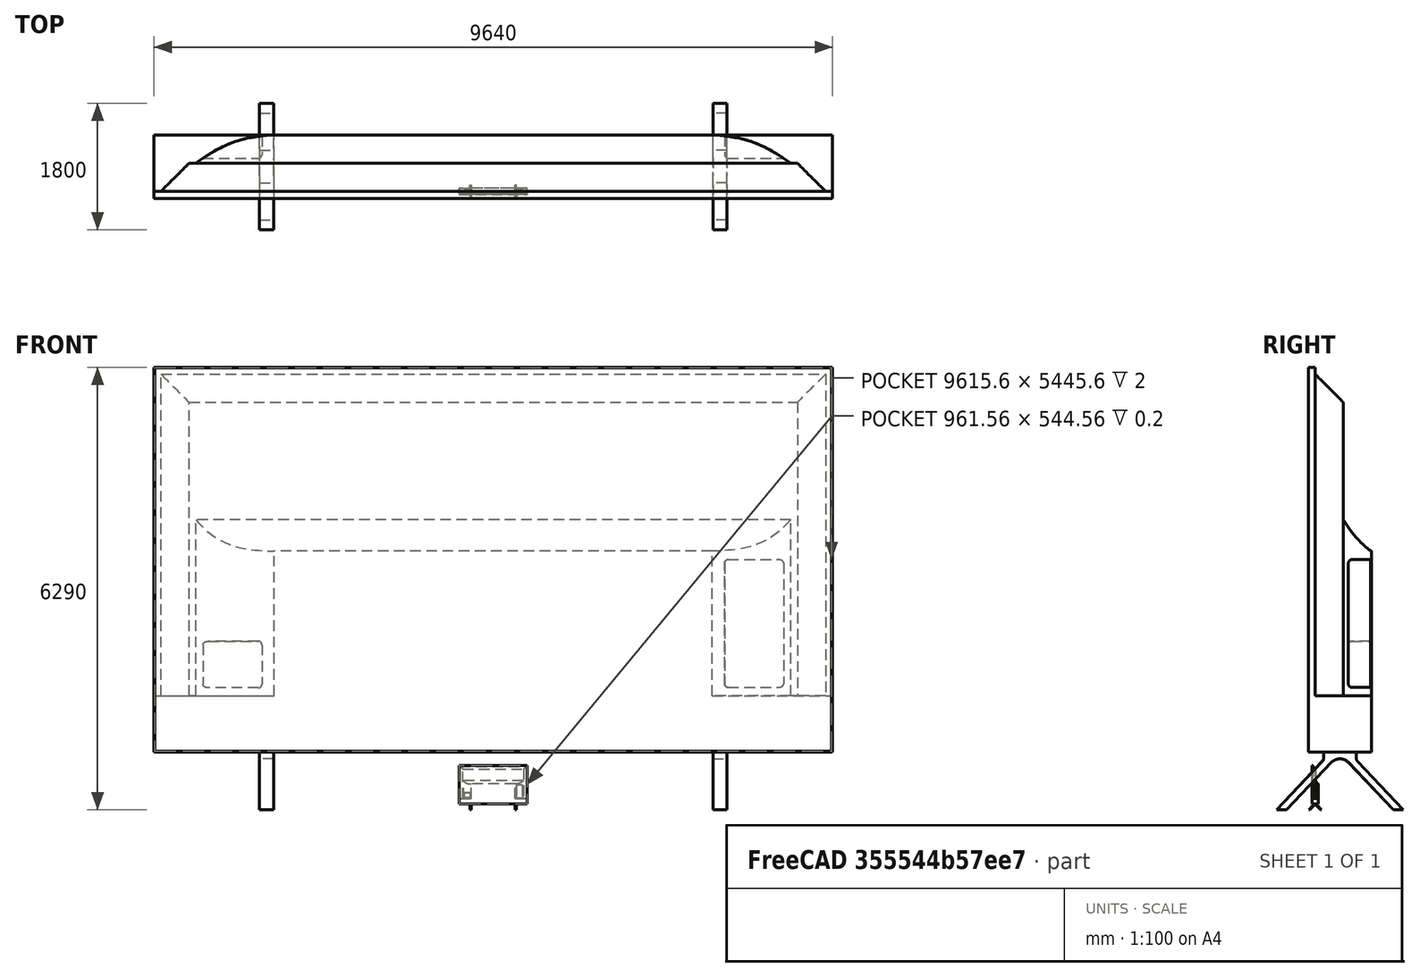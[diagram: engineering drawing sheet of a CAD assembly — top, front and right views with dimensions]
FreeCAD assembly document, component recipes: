
FREECAD ASSEMBLY — COMPONENT RECIPES ("tv")

This assembly document has 3 components, labeled P0..P2 below (a component is one placed body or linked part). 3 of them carry a construction recipe — the FreeCAD feature program that regenerates the part from scratch, quoted from this document or its linked companion documents; the rest are supplied as boundary geometry only. No exploded tour is included for this assembly.
COMPONENT P0 — recipe-attached ("Screen", modeled in this document).
Construction recipe (the document's own serialized feature program — sketch geometry with constraints, then the solid features built on it; lengths are millimeters unless a unit is written):

FEATURE [Sketcher::SketchObject] Sketch003
  ArcFitTolerance = 1e-06
  AttachmentSupport = -> [XZ_Plane]
  FullyConstrained = true
  MakeInternals = false
  MapMode = 5
  Placement = pos=(0,0,0) rot=(1,0,0;1.5708rad)
  sketch-geometry (5):
    g0: LineSegment StartX=-4820 StartY=820 StartZ=0 EndX=4820 EndY=820 EndZ=0
    g1: LineSegment StartX=4820 StartY=820 StartZ=0 EndX=4820 EndY=6290 EndZ=0
    g2: LineSegment StartX=4820 StartY=6290 StartZ=0 EndX=-4820 EndY=6290 EndZ=0
    g3: LineSegment StartX=-4820 StartY=6290 StartZ=0 EndX=-4820 EndY=820 EndZ=0
    g4: GeomPoint [constr] X=0 Y=3555 Z=0
  constraints (13):
    c: Coincident(g0,g1)
    c: Coincident(g1,g2)
    c: Coincident(g2,g3)
    c: Coincident(g3,g0)
    c: Horizontal(g0)
    c: Horizontal(g2)
    c: Vertical(g1)
    c: Vertical(g3)
    c: Symmetric(g2,g0,g4)
    c: Distance(g1,g3) = 9640
    c: PointOnObject(g4,g-2)
    c: DistanceY(g1,g1) = 5470
    c: DistanceY(g0) = 820
FEATURE [PartDesign::Pad] Pad
  Direction = (0,-1,2e-16)
  Length = 100
  Length2 = 10
  Placement = pos=(0,0,0) rot=(1,0,0;1.5708rad)
  Profile = -> Sketch003
  ReferenceAxis = -> Sketch003 [N_Axis]
  Refine = true
  Suppressed = false
  Type = 0
FEATURE [Sketcher::SketchObject] Sketch004
  ArcFitTolerance = 1e-06
  AttachmentSupport = -> [Pad]
  ExternalGeometry = -> [Pad]
  FullyConstrained = true
  MakeInternals = false
  MapMode = 5
  Placement = pos=(0,7.894e-13,0) rot=(-1,0,0;1.5708rad)
  sketch-geometry (4):
    g0: LineSegment StartX=-4820 StartY=-820 StartZ=0 EndX=-4820 EndY=-1620 EndZ=0
    g1: LineSegment StartX=-4820 StartY=-1620 StartZ=0 EndX=4820 EndY=-1620 EndZ=0
    g2: LineSegment StartX=4820 StartY=-1620 StartZ=0 EndX=4820 EndY=-820 EndZ=0
    g3: LineSegment StartX=4820 StartY=-820 StartZ=0 EndX=-4820 EndY=-820 EndZ=0
  constraints (10):
    c: Coincident(g0,g1)
    c: Coincident(g1,g2)
    c: Coincident(g2,g3)
    c: Coincident(g3,g0)
    c: Vertical(g0)
    c: Vertical(g2)
    c: Horizontal(g1)
    c: DistanceY(g0,g0) = 800
    c: Coincident(g2,g-3)
    c: Coincident(g0,g-4)
FEATURE [PartDesign::Pad] Pad001
  BaseFeature = -> Pad
  Direction = (0,1,2e-16)
  Length = 800
  Length2 = 10
  Placement = pos=(0,0,0) rot=(1,0,0;1.5708rad)
  Profile = -> Sketch004
  ReferenceAxis = -> Sketch004 [N_Axis]
  Refine = true
  Suppressed = false
  Type = 0
FEATURE [Sketcher::SketchObject] Sketch005
  ArcFitTolerance = 1e-06
  AttachmentSupport = -> [Pad001]
  ExternalGeometry = -> [Pad001]
  FullyConstrained = false
  MakeInternals = false
  MapMode = 5
  Placement = pos=(0,7.894e-13,0) rot=(-1,0,0;1.5708rad)
  sketch-geometry (4):
    g0: LineSegment StartX=-4720 StartY=-6190 StartZ=0 EndX=4720 EndY=-6190 EndZ=0
    g1: LineSegment StartX=4720 StartY=-6190 StartZ=0 EndX=4720 EndY=-963.315 EndZ=0
    g2: LineSegment StartX=4720 StartY=-963.315 StartZ=0 EndX=-4720 EndY=-963.315 EndZ=0
    g3: LineSegment StartX=-4720 StartY=-963.315 StartZ=0 EndX=-4720 EndY=-6190 EndZ=0
  constraints (11):
    c: Coincident(g0,g1)
    c: Coincident(g1,g2)
    c: Coincident(g2,g3)
    c: Coincident(g3,g0)
    c: Horizontal(g0)
    c: Horizontal(g2)
    c: Vertical(g1)
    c: Vertical(g3)
    c: DistanceY(g-3,g0) = 100
    c: DistanceX(g-3,g0) = 100
    c: DistanceX(g0,g-4) = 100
FEATURE [PartDesign::Pad] Pad002
  BaseFeature = -> Pad001
  Direction = (0,1,2e-16)
  Length = 400
  Length2 = 10
  Placement = pos=(0,0,0) rot=(1,0,0;1.5708rad)
  Profile = -> Sketch005
  ReferenceAxis = -> Sketch005 [N_Axis]
  Refine = true
  Suppressed = false
  TaperAngle = -45
  Type = 0
FEATURE [Sketcher::SketchObject] Sketch008
  ArcFitTolerance = 1e-06
  AttachmentSupport = -> [Pad002]
  ExternalGeometry = -> [Pad002]
  FullyConstrained = false
  MakeInternals = false
  MapMode = 5
  Placement = pos=(0,0,1620) rot=(0,0,1;3.14159rad)
  sketch-geometry (18):
    g0: LineSegment StartX=0 StartY=-400 StartZ=0 EndX=-4226.42 EndY=-400 EndZ=0
    g1: Circle [constr] CenterX=-4226.42 CenterY=-400 CenterZ=0 NormalX=0 NormalY=0 NormalZ=1 AngleXU=0 Radius=1
    g2: Circle [constr] CenterX=-3745.48 CenterY=-741.541 CenterZ=0 NormalX=0 NormalY=0 NormalZ=1 AngleXU=0 Radius=1
    g3: Circle [constr] CenterX=-3483.42 CenterY=-773.588 CenterZ=0 NormalX=0 NormalY=0 NormalZ=1 AngleXU=0 Radius=1
    g4: BSplineCurve PolesCount=4 KnotsCount=2 Degree=3 IsPeriodic=0
    g5: GeomPoint [constr] X=-4226.42 Y=-400 Z=0
    g6: GeomPoint [constr] X=-3109.89 Y=-800 Z=0
    g7: Circle [constr] CenterX=-3109.89 CenterY=-800 CenterZ=0 NormalX=0 NormalY=0 NormalZ=1 AngleXU=0 Radius=1
    g8: LineSegment StartX=-3109.89 StartY=-800 StartZ=0 EndX=0 EndY=-800 EndZ=0
    g9: Circle [constr] CenterX=4226.42 CenterY=-400 CenterZ=0 NormalX=0 NormalY=0 NormalZ=1 AngleXU=0 Radius=1
    g10: Circle [constr] CenterX=3745.48 CenterY=-741.541 CenterZ=0 NormalX=0 NormalY=0 NormalZ=1 AngleXU=0 Radius=1
    g11: Circle [constr] CenterX=3483.42 CenterY=-773.588 CenterZ=0 NormalX=0 NormalY=0 NormalZ=1 AngleXU=0 Radius=1
    g12: BSplineCurve PolesCount=4 KnotsCount=2 Degree=3 IsPeriodic=0
    g13: GeomPoint [constr] X=4226.42 Y=-400 Z=0
    g14: GeomPoint [constr] X=3109.89 Y=-800 Z=0
    g15: Circle [constr] CenterX=3109.89 CenterY=-800 CenterZ=0 NormalX=0 NormalY=0 NormalZ=1 AngleXU=0 Radius=1
    g16: LineSegment StartX=3109.89 StartY=-800 StartZ=0 EndX=0 EndY=-800 EndZ=0
    g17: LineSegment StartX=0 StartY=-400 StartZ=0 EndX=4226.42 EndY=-400 EndZ=0
  constraints (25):
    c: Horizontal(g0)
    c: PointOnObject(g0,g-3)
    c: Weight(g1) = 1
    c: Equal(g1,g2)
    c: Equal(g1,g3)
    c: InternalAlignment(g1,g4)
    c: InternalAlignment(g2,g4)
    c: InternalAlignment(g3,g4)
    c: InternalAlignment(g5,g4)
    c: InternalAlignment(g6,g4)
    c: Coincident(g1,g0)
    c: InternalAlignment(g7,g4)
    c: Equal(g7,g1)
    c: Horizontal(g17)
    c: Weight(g9) = 1
    c: Equal(g9,g10)
    c: Equal(g9,g11)
    c: InternalAlignment(g9,g12)
    c: InternalAlignment(g10,g12)
    c: InternalAlignment(g11,g12)
    c: InternalAlignment(g13,g12)
    c: InternalAlignment(g14,g12)
    c: Coincident(g9,g17)
    c: InternalAlignment(g15,g12)
    c: Equal(g15,g9)
FEATURE [PartDesign::Pad] Pad003
  BaseFeature = -> Pad002
  Direction = (0,0,1)
  Length = 2500
  Length2 = 10
  Placement = pos=(0,0,0) rot=(1,0,0;1.5708rad)
  Profile = -> Sketch008
  ReferenceAxis = -> Sketch008 [N_Axis]
  Refine = true
  Suppressed = false
  Type = 0
FEATURE [Sketcher::SketchObject] Sketch009
  ArcFitTolerance = 1e-06
  AttachmentSupport = -> [Pad003]
  ExternalGeometry = -> [Pad003]
  FullyConstrained = false
  MakeInternals = false
  MapMode = 5
  Placement = pos=(4820,-4.5308e-12,0) rot=(0.707107,0,0.707107;3.14159rad)
  sketch-geometry (8):
    g0: LineSegment StartX=4120 StartY=-800 StartZ=0 EndX=3674.07 EndY=-800 EndZ=0
    g1: Circle [constr] CenterX=4120 CenterY=-400 CenterZ=0 NormalX=0 NormalY=0 NormalZ=1 AngleXU=0 Radius=1
    g2: Circle [constr] CenterX=3794.85 CenterY=-604.641 CenterZ=0 NormalX=0 NormalY=0 NormalZ=1 AngleXU=0 Radius=1
    g3: Circle [constr] CenterX=3674.07 CenterY=-800 CenterZ=0 NormalX=0 NormalY=0 NormalZ=1 AngleXU=0 Radius=1
    g4: BSplineCurve PolesCount=3 KnotsCount=2 Degree=2 IsPeriodic=0
    g5: GeomPoint [constr] X=4120 Y=-400 Z=0
    g6: GeomPoint [constr] X=3674.07 Y=-800 Z=0
    g7: LineSegment StartX=4120 StartY=-400 StartZ=0 EndX=4120 EndY=-800 EndZ=0
  constraints (12):
    c: Coincident(g0,g-4)
    c: Horizontal(g0)
    c: Weight(g1) = 1
    c: Equal(g1,g2)
    c: Equal(g1,g3)
    c: InternalAlignment(g1,g4)
    c: InternalAlignment(g2,g4)
    c: InternalAlignment(g3,g4)
    c: InternalAlignment(g5,g4)
    c: InternalAlignment(g6,g4)
    c: Coincident(g1,g-4)
    c: Coincident(g3,g0)
FEATURE [PartDesign::Pocket] Pocket
  BaseFeature = -> Pad003
  Direction = (-1,0,2e-16)
  Length = 5
  Length2 = 5
  Placement = pos=(0,0,0) rot=(1,0,0;1.5708rad)
  Profile = -> Sketch009
  ReferenceAxis = -> Sketch009 [N_Axis]
  Refine = true
  Suppressed = false
  Type = 1
FEATURE [Sketcher::SketchObject] Sketch010
  ArcFitTolerance = 1e-06
  AttachmentSupport = -> [Pocket]
  ExternalGeometry = -> [Pocket]
  FullyConstrained = false
  MakeInternals = false
  MapMode = 5
  Placement = pos=(0,800,0) rot=(-1,0,0;1.5708rad)
  sketch-geometry (13):
    g0: LineSegment StartX=4524.01 StartY=-3554.92 StartZ=0 EndX=4524.01 EndY=-1739.15 EndZ=0
    g1: LineSegment StartX=4524.01 StartY=-1739.15 StartZ=0 EndX=3287.44 EndY=-1739.15 EndZ=0
    g2: LineSegment StartX=3287.44 StartY=-1739.15 StartZ=0 EndX=3287.44 EndY=-3554.92 EndZ=0
    g3: LineSegment StartX=3287.44 StartY=-3554.92 StartZ=0 EndX=4524.01 EndY=-3554.92 EndZ=0
    g4: LineSegment StartX=-3287.44 StartY=-2395.51 StartZ=0 EndX=-3287.44 EndY=-1732.57 EndZ=0
    g5: LineSegment StartX=-3287.44 StartY=-1732.57 StartZ=0 EndX=-4524.01 EndY=-1732.57 EndZ=0
    g6: LineSegment StartX=-4524.01 StartY=-1732.57 StartZ=0 EndX=-4524.01 EndY=-2395.51 EndZ=0
    g7: LineSegment StartX=-4524.01 StartY=-2395.51 StartZ=0 EndX=-3287.44 EndY=-2395.51 EndZ=0
    g8: LineSegment [constr] StartX=3287.44 StartY=-3554.92 StartZ=0 EndX=3109.89 EndY=-3554.92 EndZ=0
    g9: LineSegment [constr] StartX=3109.89 StartY=-3554.92 StartZ=0 EndX=3109.89 EndY=-3674.07 EndZ=0
    g10: LineSegment [constr] StartX=3287.44 StartY=-1739.15 StartZ=0 EndX=3109.89 EndY=-1739.15 EndZ=0
    g11: LineSegment [constr] StartX=3109.89 StartY=-1739.15 StartZ=0 EndX=3109.89 EndY=-1620 EndZ=0
    g12: LineSegment [constr] StartX=-3287.44 StartY=-1732.57 StartZ=0 EndX=-3109.89 EndY=-1732.57 EndZ=0
  constraints (32):
    c: Coincident(g0,g1)
    c: Coincident(g1,g2)
    c: Coincident(g2,g3)
    c: Coincident(g3,g0)
    c: Vertical(g0)
    c: Vertical(g2)
    c: Horizontal(g1)
    c: Horizontal(g3)
    c: Coincident(g4,g5)
    c: Coincident(g5,g6)
    c: Coincident(g6,g7)
    c: Coincident(g7,g4)
    c: Vertical(g4)
    c: Vertical(g6)
    c: Horizontal(g5)
    c: Horizontal(g7)
    c: Coincident(g8,g2)
    c: PointOnObject(g8,g-3)
    c: Horizontal(g8)
    c: Coincident(g9,g8)
    c: Coincident(g9,g-3)
    c: Coincident(g10,g1)
    c: PointOnObject(g10,g-3)
    c: Horizontal(g10)
    c: Coincident(g11,g10)
    c: Coincident(g11,g-3)
    c: Equal(g9,g11)
    c: Coincident(g12,g4)
    c: PointOnObject(g12,g-4)
    c: Horizontal(g12)
    c: Equal(g12,g10)
    c: Equal(g3,g7)
FEATURE [PartDesign::Pocket] Pocket001
  BaseFeature = -> Pocket
  Direction = (0,-1,-2e-16)
  Length = 330
  Length2 = 5
  Placement = pos=(0,0,0) rot=(1,0,0;1.5708rad)
  Profile = -> Sketch010
  ReferenceAxis = -> Sketch010 [N_Axis]
  Refine = true
  Suppressed = false
  Type = 0
FEATURE [PartDesign::Fillet] Fillet
  Base = -> Pocket001 [Edge54,Edge57]
  BaseFeature = -> Pocket001
  Placement = pos=(0,0,0) rot=(1,0,0;1.5708rad)
  Radius = 50
  Refine = true
  SupportTransform = false
  Suppressed = false
  UseAllEdges = false
FEATURE [PartDesign::Fillet] Fillet001
  Base = -> Fillet [Edge16,Edge1,Edge62,Edge64]
  BaseFeature = -> Fillet
  Placement = pos=(0,0,0) rot=(1,0,0;1.5708rad)
  Radius = 50
  Refine = true
  SupportTransform = false
  Suppressed = false
  UseAllEdges = false
FEATURE [Sketcher::SketchObject] Sketch011
  ArcFitTolerance = 1e-06
  AttachmentSupport = -> [Fillet001]
  ExternalGeometry = -> [Fillet001]
  FullyConstrained = true
  MakeInternals = false
  MapMode = 5
  Placement = pos=(0,-100,0) rot=(1,0,0;1.5708rad)
  sketch-geometry (4):
    g0: LineSegment StartX=-4807.8 StartY=6277.8 StartZ=0 EndX=-4807.8 EndY=832.2 EndZ=0
    g1: LineSegment StartX=-4807.8 StartY=832.2 StartZ=0 EndX=4807.8 EndY=832.2 EndZ=0
    g2: LineSegment StartX=4807.8 StartY=832.2 StartZ=0 EndX=4807.8 EndY=6277.8 EndZ=0
    g3: LineSegment StartX=4807.8 StartY=6277.8 StartZ=0 EndX=-4807.8 EndY=6277.8 EndZ=0
  constraints (12):
    c: Coincident(g0,g1)
    c: Coincident(g1,g2)
    c: Coincident(g2,g3)
    c: Coincident(g3,g0)
    c: Vertical(g0)
    c: Vertical(g2)
    c: Horizontal(g1)
    c: Horizontal(g3)
    c: DistanceY(g0,g-3) = 12.2
    c: DistanceX(g-3,g0) = 12.2
    c: DistanceX(g1,g-4) = 12.2
    c: DistanceY(g-4,g1) = 12.2
FEATURE [PartDesign::Pocket] Pocket002
  BaseFeature = -> Fillet001
  Direction = (0,1,-2e-16)
  Length = 2
  Length2 = 5
  Placement = pos=(0,0,0) rot=(1,0,0;1.5708rad)
  Profile = -> Sketch011
  ReferenceAxis = -> Sketch011 [N_Axis]
  Refine = true
  Suppressed = false
  Type = 0
FEATURE [PartDesign::Body] Body
  AllowCompound = false
  Group = -> [Sketch003,Pad,Sketch004,Pad001,Sketch005,Pad002,Sketch008,Pad003,Sketch009,Pocket,Sketch010,Pocket001,Fillet,Fillet001,Sketch011,Pocket002]
  Origin = -> Origin
  Tip = -> Pocket002
COMPONENT P1 — recipe-attached ("Right_Stand", modeled in this document).
Construction recipe (the document's own serialized feature program — sketch geometry with constraints, then the solid features built on it; lengths are millimeters unless a unit is written):

FEATURE [PartDesign::ShapeBinder] CopyFillet001
  Placement = pos=(0,0,0) rot=(1,0,0;1.5708rad)
  TraceSupport = false
FEATURE [PartDesign::Plane] DatumPlane
  AttachmentOffset = pos=(0,0,-1500) rot=(0,0,1;0rad)
  AttachmentSupport = -> [CopyFillet001]
  Length = 6989.3
  MapMode = 5
  Placement = pos=(3320,0,3.331e-13) rot=(0.707107,0,0.707107;3.14159rad)
  ResizeMode = 0
  Width = 2474.3
FEATURE [Sketcher::SketchObject] Sketch006
  ArcFitTolerance = 1e-06
  AttachmentSupport = -> [DatumPlane]
  ExternalGeometry = -> [CopyFillet001]
  FullyConstrained = false
  MakeInternals = false
  MapMode = 5
  Placement = pos=(3320,0,3.331e-13) rot=(0.707107,0,0.707107;3.14159rad)
  sketch-geometry (17):
    g0: LineSegment StartX=820 StartY=-119.068 StartZ=0 EndX=820 EndY=-580.932 EndZ=0
    g1: LineSegment StartX=820 StartY=-119.068 StartZ=0 EndX=736.366 EndY=-119.068 EndZ=0
    g2: LineSegment StartX=820 StartY=-580.932 StartZ=0 EndX=742.416 EndY=-580.932 EndZ=0
    g3: LineSegment StartX=680.048 StartY=-96.5682 StartZ=0 EndX=0 EndY=550 EndZ=0
    g4: LineSegment StartX=686.36 StartY=-603.183 StartZ=0 EndX=0 EndY=-1250 EndZ=0
    g5: LineSegment [constr] StartX=820 StartY=-350 StartZ=0 EndX=0 EndY=-350 EndZ=0
    g6: LineSegment [constr] StartX=820 StartY=100 StartZ=0 EndX=820 EndY=-119.068 EndZ=0
    g7: LineSegment [constr] StartX=820 StartY=-580.932 StartZ=0 EndX=820 EndY=-800 EndZ=0
    g8: LineSegment StartX=0 StartY=408.983 StartZ=0 EndX=671.046 EndY=-229.026 EndZ=0
    g9: LineSegment StartX=670.497 StartY=-477.115 StartZ=0 EndX=0 EndY=-1108.98 EndZ=0
    g10: ArcOfCircle CenterX=553.355 CenterY=-352.811 CenterZ=0 NormalX=0 NormalY=0 NormalZ=1 AngleXU=0 Radius=170.803 StartAngle=5.46813 EndAngle=7.09382
    g11: LineSegment StartX=0 StartY=550 StartZ=0 EndX=0 EndY=408.983 EndZ=0
    g12: LineSegment StartX=0 StartY=-1108.98 StartZ=0 EndX=0 EndY=-1250 EndZ=0
    g13: ArcOfCircle CenterX=736.366 CenterY=-37.3338 CenterZ=0 NormalX=0 NormalY=0 NormalZ=1 AngleXU=0 Radius=81.7339 StartAngle=3.95222 EndAngle=4.71239
    g14: GeomPoint [constr] X=703.713 Y=-119.068 Z=0
    g15: ArcOfCircle CenterX=742.416 CenterY=-662.666 CenterZ=0 NormalX=0 NormalY=0 NormalZ=1 AngleXU=0 Radius=81.7339 StartAngle=1.5708 EndAngle=2.32654
    g16: GeomPoint [constr] X=709.972 Y=-580.932 Z=0
  constraints (37):
    c: PointOnObject(g0,g-3)
    c: PointOnObject(g0,g-3)
    c: Coincident(g1,g0)
    c: Horizontal(g1)
    c: Coincident(g2,g0)
    c: Horizontal(g2)
    c: PointOnObject(g3,g-2)
    c: DistanceY(g4,g3) = 1800
    c: PointOnObject(g4,g-2)
    c: Symmetric(g0,g0,g5)
    c: Horizontal(g5)
    c: Symmetric(g4,g3,g5)
    c: Coincident(g6,g-3)
    c: Coincident(g6,g0)
    c: Coincident(g7,g0)
    c: Coincident(g7,g-3)
    c: Equal(g7,g6)
    c: PointOnObject(g8,g-2)
    c: PointOnObject(g9,g-2)
    c: Parallel(g8,g3)
    c: Parallel(g9,g4)
    c: Tangent(g8,g10) = 1.5708
    c: Tangent(g9,g10) = 1.5708
    c: Coincident(g11,g3)
    c: Coincident(g11,g8)
    c: Coincident(g12,g9)
    c: Coincident(g12,g4)
    c: PointOnObject(g14,g1)
    c: PointOnObject(g14,g3)
    c: Tangent(g1,g13) = 1.5708
    c: Tangent(g3,g13) = 1.5708
    c: PointOnObject(g16,g2)
    c: PointOnObject(g16,g4)
    c: Tangent(g2,g15) = -1.5708
    c: Tangent(g4,g15) = -1.5708
    c: Equal(g13,g15)
    c: Equal(g12,g11)
FEATURE [PartDesign::Pad] Pad004
  Direction = (1,0,-2e-16)
  Length = 200
  Length2 = 10
  Placement = pos=(3320,0,3.331e-13) rot=(0.707107,0,0.707107;3.14159rad)
  Profile = -> Sketch006
  ReferenceAxis = -> Sketch006 [N_Axis]
  Refine = true
  Reversed = true
  Suppressed = false
  Type = 0
FEATURE [PartDesign::Body] Body001
  AllowCompound = false
  Group = -> [DatumPlane,CopyFillet001,Sketch006,Pad004]
  Origin = -> Origin001
  Tip = -> Pad004
COMPONENT P2 — recipe-attached ("Left_Stand", modeled in this document).
Construction recipe (the document's own serialized feature program — sketch geometry with constraints, then the solid features built on it; lengths are millimeters unless a unit is written):

FEATURE [PartDesign::ShapeBinder] CopyFillet002
  Placement = pos=(0,0,0) rot=(1,0,0;1.5708rad)
  TraceSupport = false
FEATURE [PartDesign::Plane] DatumPlane001
  AttachmentOffset = pos=(0,0,-1500) rot=(0,0,1;0rad)
  AttachmentSupport = -> [CopyFillet002]
  Length = 6989.3
  MapMode = 5
  Placement = pos=(-3320,0,3.331e-13) rot=(0.707107,0,-0.707107;3.14159rad)
  ResizeMode = 0
  Width = 2474.3
FEATURE [Sketcher::SketchObject] Sketch007
  ArcFitTolerance = 1e-06
  AttachmentSupport = -> [DatumPlane001]
  FullyConstrained = false
  MakeInternals = false
  MapMode = 5
  Placement = pos=(-3320,0,3.331e-13) rot=(0.707107,0,-0.707107;3.14159rad)
  sketch-geometry (17):
    g0: LineSegment StartX=-820 StartY=-580.932 StartZ=0 EndX=-820 EndY=-119.068 EndZ=0
    g1: LineSegment StartX=-820 StartY=-580.932 StartZ=0 EndX=-736.366 EndY=-580.932 EndZ=0
    g2: LineSegment StartX=-820 StartY=-119.068 StartZ=0 EndX=-742.416 EndY=-119.068 EndZ=0
    g3: LineSegment StartX=-680.048 StartY=-603.432 StartZ=0 EndX=0 EndY=-1250 EndZ=0
    g4: LineSegment StartX=-686.36 StartY=-96.8166 StartZ=0 EndX=0 EndY=550 EndZ=0
    g5: LineSegment [constr] StartX=-820 StartY=-350 StartZ=0 EndX=0 EndY=-350 EndZ=0
    g6: LineSegment [constr] StartX=-820 StartY=-800 StartZ=0 EndX=-820 EndY=-580.932 EndZ=0
    g7: LineSegment [constr] StartX=-820 StartY=-119.068 StartZ=0 EndX=-820 EndY=100 EndZ=0
    g8: LineSegment StartX=0 StartY=-1108.98 StartZ=0 EndX=-671.046 EndY=-470.974 EndZ=0
    g9: LineSegment StartX=-670.497 StartY=-222.885 StartZ=0 EndX=0 EndY=408.983 EndZ=0
    g10: ArcOfCircle CenterX=-553.355 CenterY=-347.189 CenterZ=0 NormalX=0 NormalY=0 NormalZ=1 AngleXU=0 Radius=170.803 StartAngle=2.32654 EndAngle=3.95222
    g11: LineSegment StartX=0 StartY=-1250 StartZ=0 EndX=0 EndY=-1108.98 EndZ=0
    g12: LineSegment StartX=0 StartY=408.983 StartZ=0 EndX=0 EndY=550 EndZ=0
    g13: ArcOfCircle CenterX=-736.366 CenterY=-662.666 CenterZ=0 NormalX=0 NormalY=0 NormalZ=1 AngleXU=0 Radius=81.734 StartAngle=0.81063 EndAngle=1.5708
    g14: GeomPoint [constr] X=-703.713 Y=-580.932 Z=0
    g15: ArcOfCircle CenterX=-742.416 CenterY=-37.3338 CenterZ=0 NormalX=0 NormalY=0 NormalZ=1 AngleXU=0 Radius=81.734 StartAngle=4.71239 EndAngle=5.46813
    g16: GeomPoint [constr] X=-709.972 Y=-119.068 Z=0
  constraints (25):
    c: Coincident(g1,g0)
    c: Coincident(g2,g0)
    c: Symmetric(g0,g0,g5)
    c: Symmetric(g4,g3,g5)
    c: Coincident(g6,g0)
    c: Coincident(g7,g0)
    c: Equal(g7,g6)
    c: Parallel(g8,g3)
    c: Parallel(g9,g4)
    c: Tangent(g8,g10) = 1.5708
    c: Tangent(g9,g10) = 1.5708
    c: Coincident(g11,g3)
    c: Coincident(g11,g8)
    c: Coincident(g12,g9)
    c: Coincident(g12,g4)
    c: PointOnObject(g14,g1)
    c: PointOnObject(g14,g3)
    c: Tangent(g1,g13) = 1.5708
    c: Tangent(g3,g13) = 1.5708
    c: PointOnObject(g16,g2)
    c: PointOnObject(g16,g4)
    c: Tangent(g2,g15) = -1.5708
    c: Tangent(g4,g15) = -1.5708
    c: Equal(g13,g15)
    c: Equal(g12,g11)
FEATURE [PartDesign::Pad] Pad005
  Direction = (-1,0,-2e-16)
  Length = 200
  Length2 = 10
  Placement = pos=(-3320,0,3.331e-13) rot=(0.707107,0,-0.707107;3.14159rad)
  Profile = -> Sketch007
  ReferenceAxis = -> Sketch007 [N_Axis]
  Refine = true
  Reversed = true
  Suppressed = false
  Type = 0
FEATURE [PartDesign::Body] Body002
  AllowCompound = false
  Group = -> [DatumPlane001,CopyFillet002,Sketch007,Pad005]
  Origin = -> Origin002
  Tip = -> Pad005
PROVENANCE & LICENSES
A FreeCAD (.FCStd) document from a public repository crawl; recipes are the document's own serialized feature recipes (and, for linked parts, companion documents' recipes).
License: as declared in the source repository (recorded in the dataset sidecar).
